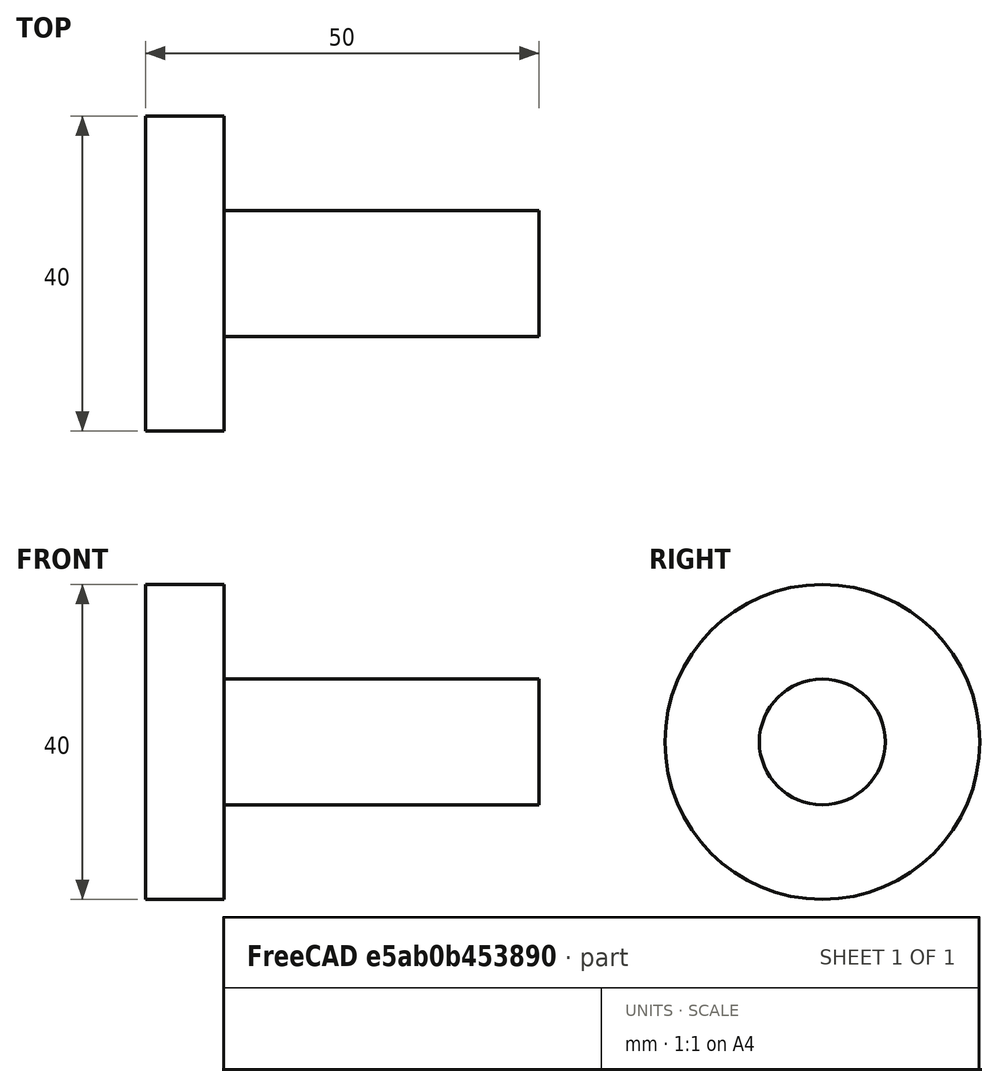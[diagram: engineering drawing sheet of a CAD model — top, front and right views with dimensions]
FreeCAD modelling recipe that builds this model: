
FCSTD DOCUMENT  (FreeCAD 0.18.4R)
Label: wheels
License: All rights reserved
LicenseURL: http://en.wikipedia.org/wiki/All_rights_reserved
objects: Sketcher::SketchObject×1, PartDesign::Revolution×1, PartDesign::Body×1
note: 4 computed .brp shape members not serialized (recipe doc carries the construction recipe); baked Part::Feature solids carry a one-line shape summary decoded from their .brp

FEATURE [Sketcher::SketchObject] Sketch
  Placement = pos=(0,0,0) rot=(1,0,0;1.5708rad)
  sketch-geometry (6):
    g0: LineSegment StartX=0 StartY=0 StartZ=0 EndX=50 EndY=0 EndZ=0
    g1: LineSegment StartX=50 StartY=0 StartZ=0 EndX=50 EndY=8 EndZ=0
    g2: LineSegment StartX=50 StartY=8 StartZ=0 EndX=10 EndY=8 EndZ=0
    g3: LineSegment StartX=10 StartY=8 StartZ=0 EndX=10 EndY=20 EndZ=0
    g4: LineSegment StartX=10 StartY=20 StartZ=0 EndX=0 EndY=20 EndZ=0
    g5: LineSegment StartX=0 StartY=20 StartZ=0 EndX=0 EndY=0 EndZ=0
  constraints (17):
    c: Coincident(g-1,g0)
    c: PointOnObject(g0,g-1)
    c: Coincident(g0,g1)
    c: Vertical(g1)
    c: Coincident(g1,g2)
    c: Horizontal(g2)
    c: Coincident(g2,g3)
    c: Vertical(g3)
    c: Coincident(g3,g4)
    c: Horizontal(g4)
    c: Coincident(g4,g5)
    c: Coincident(g5,g0)
    c: Vertical(g5)
    c: Distance(g1) = 8
    c: Distance(g5) = 20
    c: Distance(g4) = 10
    c: Distance(g0) = 50
FEATURE [PartDesign::Revolution] Revolution
  Angle = 360
  Axis = (1,0,0)
  Base = (0,0,0)
  Placement = pos=(0,0,0) rot=(1,0,0;1.5708rad)
  Profile = -> Sketch
  ReferenceAxis = -> X_Axis
FEATURE [PartDesign::Body] Body
  Group = -> [Sketch,Revolution]
  Origin = -> Origin
  Tip = -> Revolution
